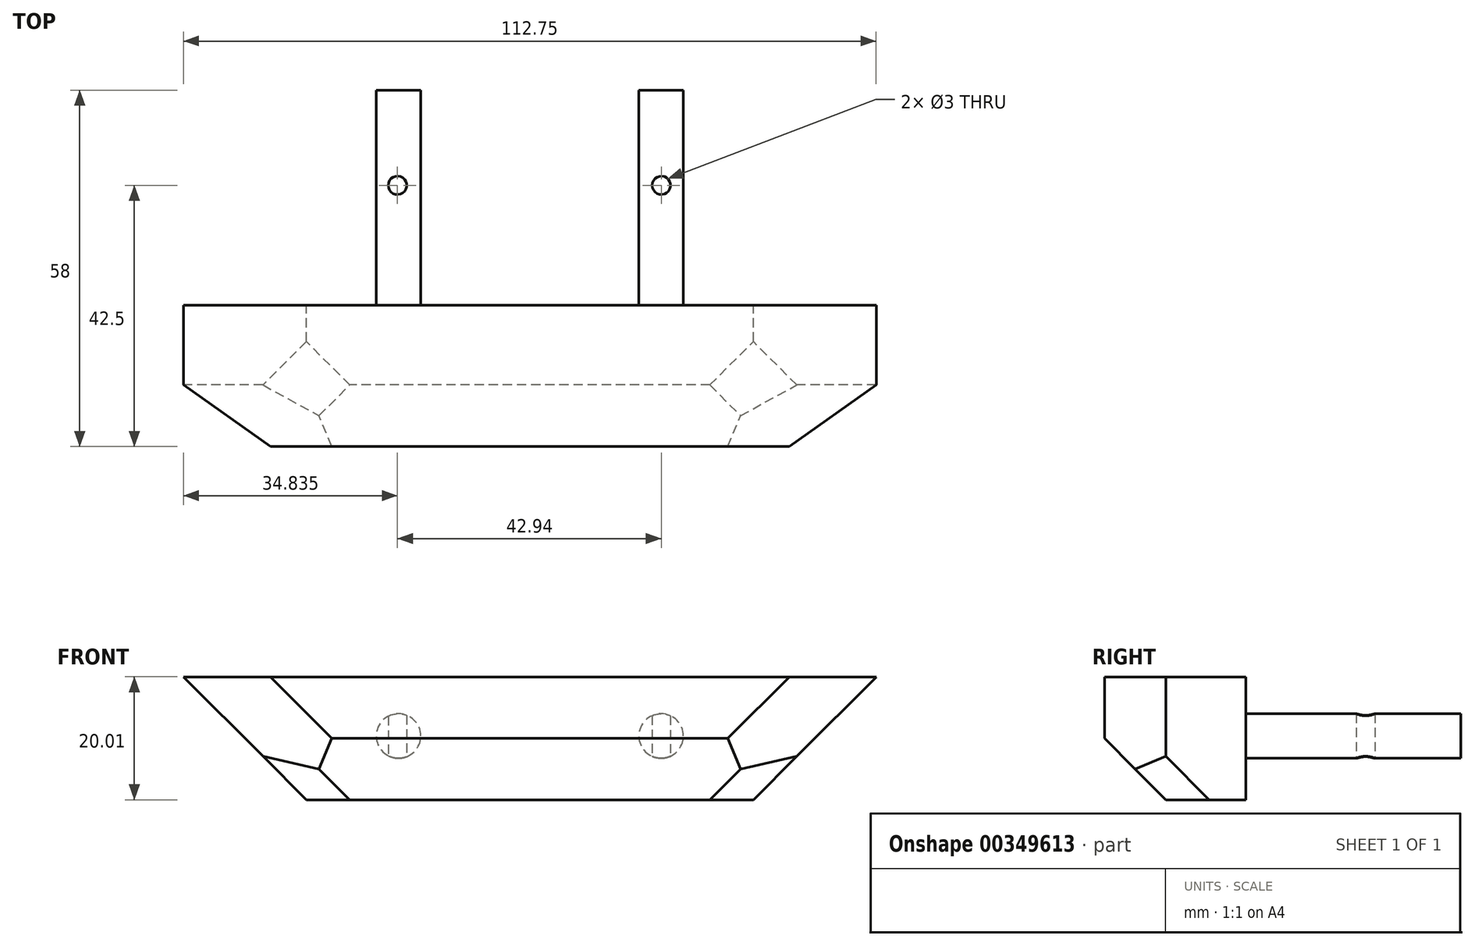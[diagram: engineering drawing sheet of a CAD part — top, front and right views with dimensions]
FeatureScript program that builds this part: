
annotation { "Feature Type Name" : "Feature", "Feature Type Description" : "" }
export const myFeature = defineFeature(function(context is Context, id is Id, definition is map)
    precondition{}
    {
        {
            var Q0;
            Q0=qCreatedBy(makeId("Front.planeOp"),FACE);
            var sketch = newSketch(context, id + "F0", { "sketchPlane" : qUnion([Q0])});
            skCircle(sketch, "E0", {"center": v(-21.2, 0) * mm, "radius": 3.62 * mm});
            skCircle(sketch, "E1", {"center": v(21.54, 0) * mm, "radius": 3.62 * mm});
            skLineSegment(sketch, "E2", {"start": v(-56.2, 9.62) * mm, "end": v(56.54, 9.62) * mm});
            skLineSegment(sketch, "E3", {"start": v(-36.2, -10.38) * mm, "end": v(36.54, -10.38) * mm});
            skLineSegment(sketch, "E4", {"start": v(-56.2, 9.62) * mm, "end": v(-36.2, -10.38) * mm});
            skLineSegment(sketch, "E5", {"start": v(56.54, 9.62) * mm, "end": v(36.54, -10.38) * mm});
            skSolve(sketch);
        }
        {
            var Q0;
            Q0 = qSketchRegion(id + "F0", true);
            var Q1;
            Q1=makeQuery(id+"F0.imprint","IMPRINT",FACE,{"disambiguationData":[TD([[makeQuery(id+"F0.imprint","IMPRINT",EDGE,{"derivedFrom":sQuery(id+"F0.wireOp",EDGE,"E0")}),1.0]])]});
            var Q2;
            Q2=makeQuery(id+"F0.imprint","IMPRINT",FACE,{"disambiguationData":[TD([[makeQuery(id+"F0.imprint","IMPRINT",EDGE,{"derivedFrom":sQuery(id+"F0.wireOp",EDGE,"E1")}),1.0]])]});
            extrude(context, id + "F1", {"entities" : qUnion([Q0, Q1, Q2]), "depth" : 23 * mm});
        }
        {
            var Q0;
            Q0=makeQuery(id+"F0.imprint","IMPRINT",FACE,{"disambiguationData":[TD([[makeQuery(id+"F0.imprint","IMPRINT",EDGE,{"derivedFrom":sQuery(id+"F0.wireOp",EDGE,"E1")}),1.0]])]});
            var Q1;
            Q1=makeQuery(id+"F0.imprint","IMPRINT",FACE,{"disambiguationData":[TD([[makeQuery(id+"F0.imprint","IMPRINT",EDGE,{"derivedFrom":sQuery(id+"F0.wireOp",EDGE,"E0")}),1.0]])]});
            extrude(context, id + "F2", {"entities" : qUnion([Q0, Q1]), "operationType" : NewBodyOperationType.ADD, "oppositeDirection" : true, "depth" : 35 * mm});
        }
        {
            var Q0;
            Q0=qCreatedBy(makeId("Top.planeOp"),FACE);
            var sketch = newSketch(context, id + "F3", { "sketchPlane" : qUnion([Q0])});
            skLineSegment(sketch, "E6.bottom", {"start": v(17.9, 35) * mm, "end": v(25.16, 35) * mm});
            skLineSegment(sketch, "E6.top", {"start": v(17.9, 0) * mm, "end": v(25.16, 0) * mm});
            skLineSegment(sketch, "E6.left", {"start": v(17.9, 35) * mm, "end": v(17.9, 0) * mm});
            skLineSegment(sketch, "E6.right", {"start": v(25.16, 35) * mm, "end": v(25.16, 0) * mm});
            skLineSegment(sketch, "E7.bottom", {"start": v(-24.83, 35) * mm, "end": v(-17.58, 35) * mm});
            skLineSegment(sketch, "E7.top", {"start": v(-24.83, 0) * mm, "end": v(-17.58, 0) * mm});
            skLineSegment(sketch, "E7.left", {"start": v(-24.83, 35) * mm, "end": v(-24.83, 0) * mm});
            skLineSegment(sketch, "E7.right", {"start": v(-17.58, 35) * mm, "end": v(-17.58, 0) * mm});
            skCircle(sketch, "E8", {"center": v(-21.37, 19.5) * mm, "radius": 1.5 * mm});
            skCircle(sketch, "E9", {"center": v(21.57, 19.5) * mm, "radius": 1.5 * mm});
            skSolve(sketch);
        }
        {
            var Q0;
            Q0=makeQuery(id+"F3.imprint","IMPRINT",FACE,{"disambiguationData":[TD([[makeQuery(id+"F3.imprint","IMPRINT",EDGE,{"derivedFrom":sQuery(id+"F3.wireOp",EDGE,"E8")}),1.0]])]});
            var Q1;
            Q1=makeQuery(id+"F3.imprint","IMPRINT",FACE,{"disambiguationData":[TD([[makeQuery(id+"F3.imprint","IMPRINT",EDGE,{"derivedFrom":sQuery(id+"F3.wireOp",EDGE,"E9")}),1.0]])]});
            extrude(context, id + "F4", {"entities" : qUnion([Q0, Q1]), "operationType" : NewBodyOperationType.REMOVE, "endBound" : BoundingType.SYMMETRIC, "depth" : 25 * mm});
        }
        {
            var Q0;
            Q0=makeQuery(id+"F1.opExtrude","CAP_EDGE",EDGE,{"disambiguationData":[OSD([sQuery(id+"F0.wireOp",EDGE,"E3")])],"isStart":false});
            chamfer(context, id + "F5", {"entities" : qUnion([Q0]), "width" : 10 * mm, "tangentPropagation" : true});
        }
        {
            var Q0;
            Q0=makeQuery(id+"F1.opExtrude","CAP_EDGE",EDGE,{"disambiguationData":[OSD([sQuery(id+"F0.wireOp",EDGE,"E4")])],"isStart":false});
            var Q1;
            Q1=makeQuery(id+"F5.opChamfer","BLEND_EDGE",EDGE,{"blendedFrom":[makeQuery(id+"F1.opExtrude","CAP_EDGE",EDGE,{"disambiguationData":[OSD([sQuery(id+"F0.wireOp",EDGE,"E3")])],"isStart":false}),makeQuery(id+"F1.opExtrude","SWEPT_FACE",FACE,{"disambiguationData":[OSD([sQuery(id+"F0.wireOp",EDGE,"E4")])]})],"blendedInto":[makeQuery(id+"F1.opExtrude","SWEPT_FACE",FACE,{"disambiguationData":[OSD([sQuery(id+"F0.wireOp",EDGE,"E4")])]})]});
            var Q2;
            Q2=makeQuery(id+"F1.opExtrude","CAP_EDGE",EDGE,{"disambiguationData":[OSD([sQuery(id+"F0.wireOp",EDGE,"E5")])],"isStart":false});
            var Q3;
            Q3=makeQuery(id+"F5.opChamfer","BLEND_EDGE",EDGE,{"blendedFrom":[makeQuery(id+"F1.opExtrude","CAP_EDGE",EDGE,{"disambiguationData":[OSD([sQuery(id+"F0.wireOp",EDGE,"E3")])],"isStart":false}),makeQuery(id+"F1.opExtrude","SWEPT_FACE",FACE,{"disambiguationData":[OSD([sQuery(id+"F0.wireOp",EDGE,"E5")])]})],"blendedInto":[makeQuery(id+"F1.opExtrude","SWEPT_FACE",FACE,{"disambiguationData":[OSD([sQuery(id+"F0.wireOp",EDGE,"E5")])]})]});
            chamfer(context, id + "F6", {"entities" : qUnion([Q0, Q1, Q2, Q3]), "width" : 10 * mm, "tangentPropagation" : true});
        }
    });
